# Revit family: REC-MPA01
name_source: partatom
category: Structural Connections
units: mm (PartAtom-declared; Revit-internal decimal feet)

## family parameters
Cut with Voids When Loaded = Yes
Enable Cutting in Views = Yes
Host = Face
Material for Model Behavior = Steel
Shared = No

## types (1)
- MPA01
    Classification.Uniclass.Pr.Description = Brackets
    Classification.Uniclass.Pr.Number = Pr_20_85_09
    Cost = 0 $
    Creado por: = Deliprogal SL
    Default Elevation = 0 mm  [stored 0 ft]
    Description = Panel corbel model.1
    Description_ESP = Ménsula de panel modelo 1
    Export Type to IFC As = IfcElementAssembly
    Fecha Ultima Revision: = 01/03/2024
    Fecha de Creacion: = 01/03/2024
    IFCExportAs = IfcElementAssembly
    IFCExportType = Brackets
    Keynote = Supporting system of precast concrete panels on horizontal support to transmit both vertical loads (up to 43 KN) and horizontal loads (up to 8 KN).
    Keynote_ESP = Sistema de sustentación de paneles prefabricados de hormigón sobre soporte horizontal para transmitir tanto cargas verticales (hasta 43 KN) como horizontales (hasta 8 KN).
    Manufacturer = RECENSE
    Model = MPA01
    Type IFC Predefined Type = Brackets
    URL = https://recense.com
    Visible = Yes

note: [stored X ft] marks values corroborated as IEEE doubles in the binary element streams (Revit-internal decimal feet)

## geometry (parser evidence)
native form markers: Sweep x3
no freeform markers — native parametric forms only
